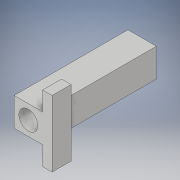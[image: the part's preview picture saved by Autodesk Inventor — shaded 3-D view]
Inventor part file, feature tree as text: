
AUTODESK INVENTOR PART (.ipt)
format: ipt  version: 2017.3 (Build 213256000, 256)  size: 107,008 bytes
history: native  units: in
note: dims shown in document units (in); Inventor stores cm internally (conversion verified against a paired STEP export)
features: extrude x3, sketch x3
ambient origin geometry x8: Origin, YZ Plane, XZ Plane, XY Plane, X Axis, Y Axis, Z Axis, Center Point
bodies: Solid1 (feature_tree)
feature tree (6):
  extrude  "Extrusion1"  Depth=0.375in
  extrude  "Extrusion2"  Depth=0.25in
  extrude  "Extrusion3"  Depth=0.25in
  sketch  "Sketch1"  dims[d0=0.375in d1=0.375in]
  sketch  "Sketch2"  dims[d2=1.5in d3=0.0in d4=0.25in]
  sketch  "Sketch3"  dims[d5=1.5in d6=0.0in d7=0.25in d8=0.875in d9=0.125in d10=0.0in]
